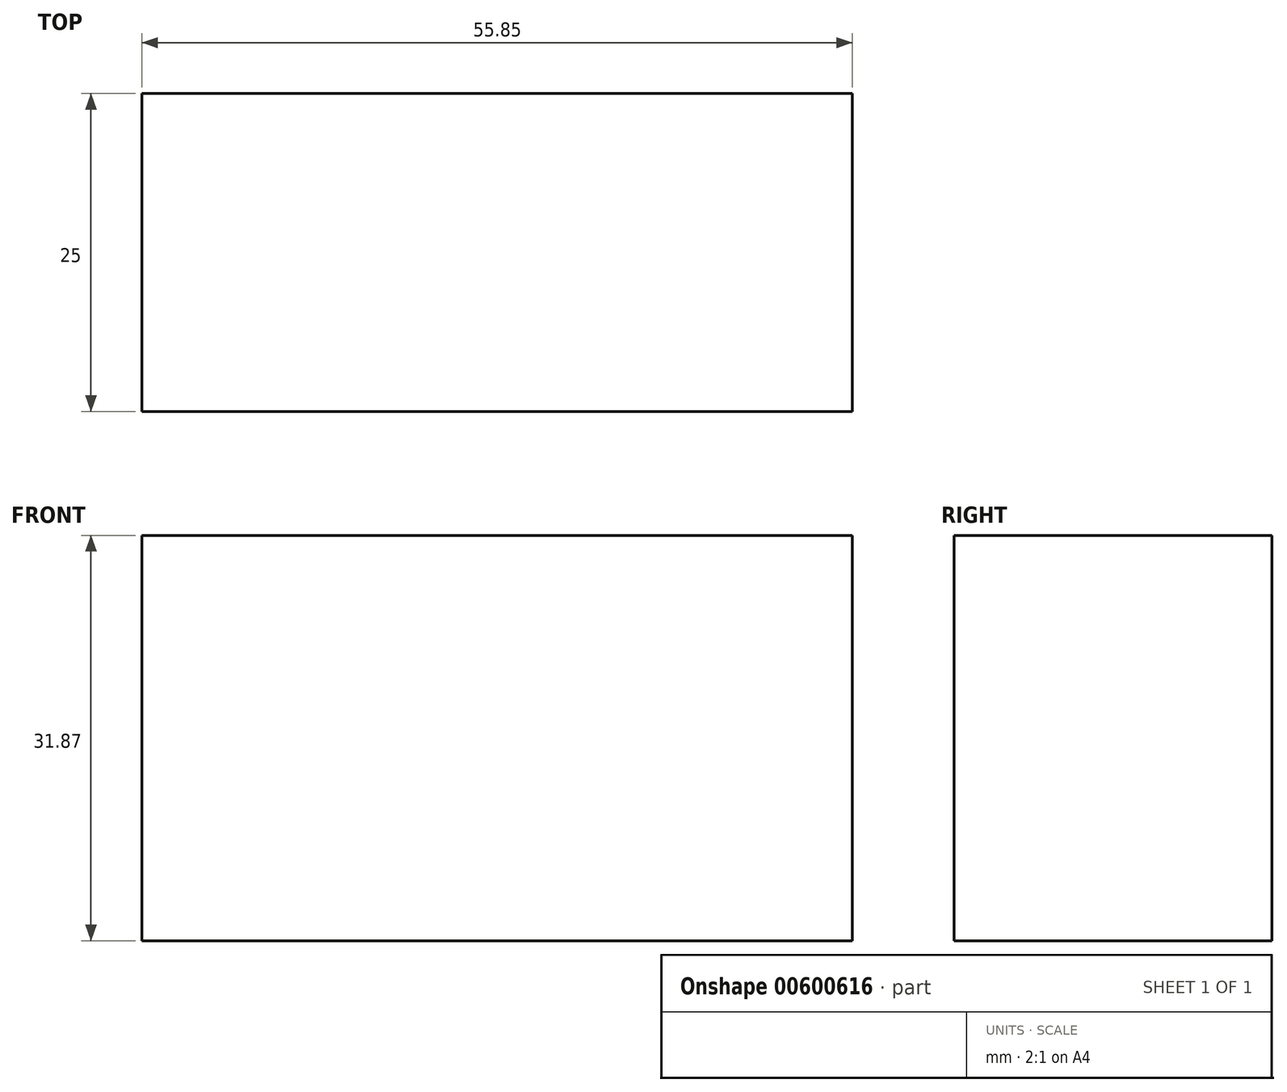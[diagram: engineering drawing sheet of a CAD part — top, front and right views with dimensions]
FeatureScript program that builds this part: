
annotation { "Feature Type Name" : "Feature", "Feature Type Description" : "" }
export const myFeature = defineFeature(function(context is Context, id is Id, definition is map)
    precondition{}
    {
        {
            var Q0;
            Q0=qCreatedBy(makeId("Front.planeOp"),FACE);
            var sketch = newSketch(context, id + "F0", { "sketchPlane" : qUnion([Q0])});
            skLineSegment(sketch, "E0.bottom", {"start": v(-93.4, 65.2) * mm, "end": v(-37.54, 65.2) * mm});
            skLineSegment(sketch, "E0.top", {"start": v(-93.4, 33.34) * mm, "end": v(-37.54, 33.34) * mm});
            skLineSegment(sketch, "E0.left", {"start": v(-93.4, 65.2) * mm, "end": v(-93.4, 33.34) * mm});
            skLineSegment(sketch, "E0.right", {"start": v(-37.54, 65.2) * mm, "end": v(-37.54, 33.34) * mm});
            skSolve(sketch);
        }
        {
            var Q0;
            Q0 = qSketchRegion(id + "F0", true);
            extrude(context, id + "F1", {"entities" : qUnion([Q0]), "depth" : 25 * mm, "offsetDistance" : 25 * mm});
        }
    });
